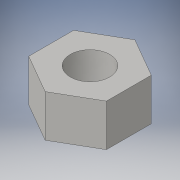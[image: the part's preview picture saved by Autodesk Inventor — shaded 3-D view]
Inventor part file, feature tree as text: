
AUTODESK INVENTOR PART (.ipt)
format: ipt  version: 2016 (Build 200138000, 138)  size: 92,160 bytes
history: native  units: in
note: dims shown in document units (in); Inventor stores cm internally (conversion verified against a paired STEP export)
features: extrude x1, sketch x1
ambient origin geometry x8: Origin, YZ Plane, XZ Plane, XY Plane, X Axis, Y Axis, Z Axis, Center Point
bodies: Solid1 (feature_tree)
feature tree (2):
  extrude  "Extrusion1"  Depth=0.375in
  sketch  "Sketch1"  dims[d0=0.19in d1=0.375in d2=0.203in d3=0.0in]
